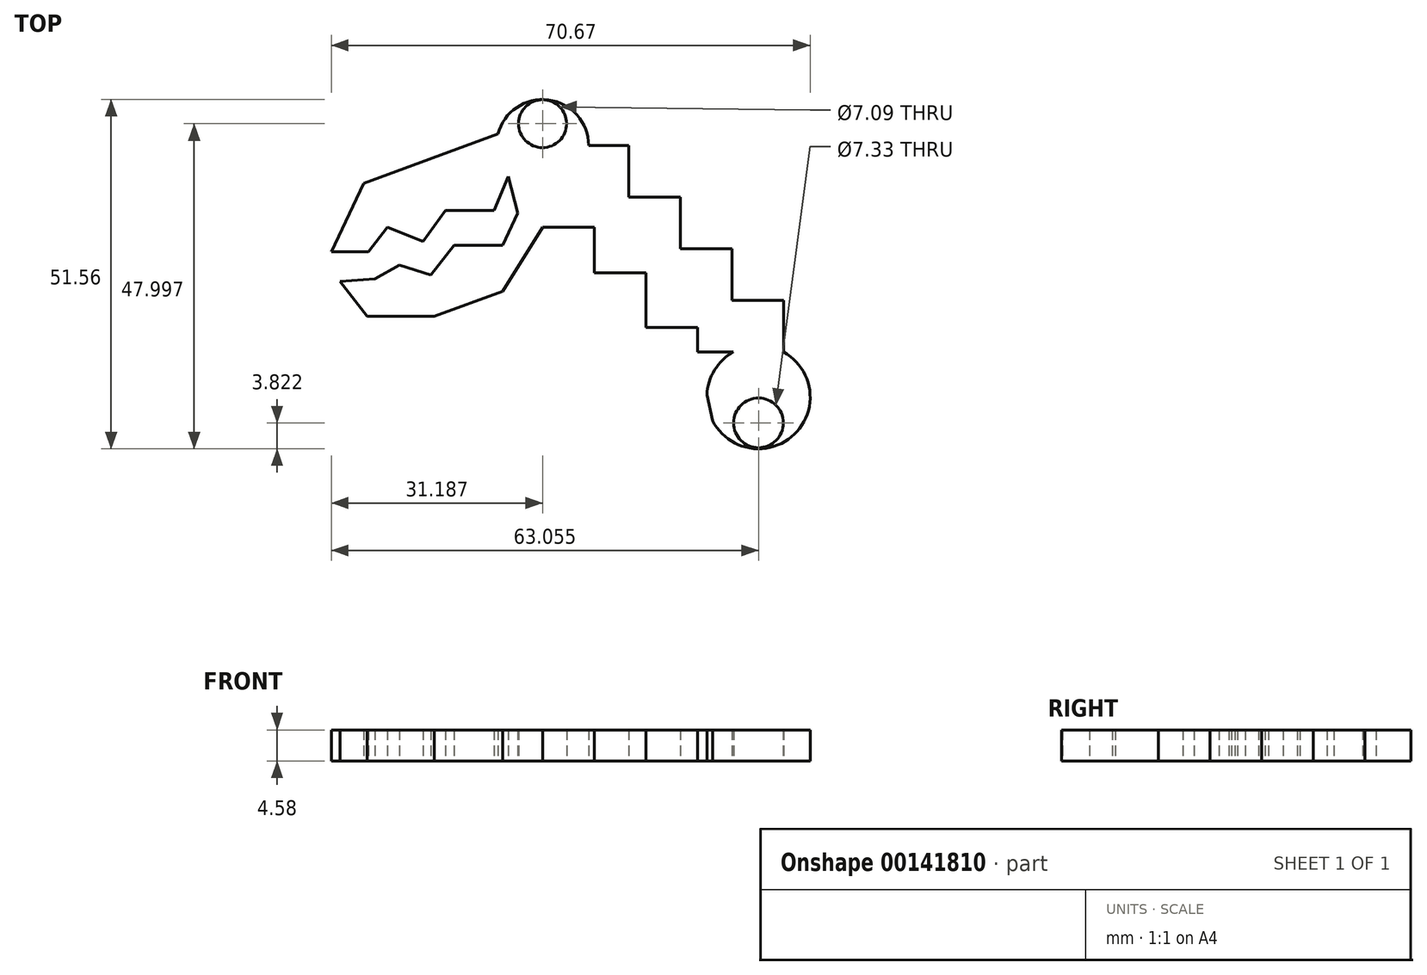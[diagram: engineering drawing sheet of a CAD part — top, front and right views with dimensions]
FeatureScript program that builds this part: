
annotation { "Feature Type Name" : "Feature", "Feature Type Description" : "" }
export const myFeature = defineFeature(function(context is Context, id is Id, definition is map)
    precondition{}
    {
        {
            var Q0;
            Q0=qCreatedBy(makeId("Top.planeOp"),FACE);
            var sketch = newSketch(context, id + "F0", { "sketchPlane" : qUnion([Q0])});
            skLineSegment(sketch, "E0", {"start": v(6.99, 43.15) * mm, "end": v(6.99, 35.53) * mm});
            skLineSegment(sketch, "E1", {"start": v(6.99, 35.53) * mm, "end": v(14.6, 35.53) * mm});
            skLineSegment(sketch, "E2", {"start": v(14.6, 35.53) * mm, "end": v(14.6, 27.9) * mm});
            skLineSegment(sketch, "E3", {"start": v(14.6, 27.9) * mm, "end": v(22.23, 27.9) * mm});
            skLineSegment(sketch, "E4", {"start": v(22.23, 27.9) * mm, "end": v(22.23, 20.29) * mm});
            skLineSegment(sketch, "E5", {"start": v(22.23, 20.29) * mm, "end": v(29.85, 20.29) * mm});
            skLineSegment(sketch, "E6", {"start": v(29.85, 20.29) * mm, "end": v(29.85, 12.67) * mm});
            skLineSegment(sketch, "E7", {"start": v(29.85, 12.67) * mm, "end": v(-5.71, 12.67) * mm});
            skLineSegment(sketch, "E8", {"start": v(-5.71, 12.67) * mm, "end": v(-5.71, 43.15) * mm});
            skLineSegment(sketch, "E9", {"start": v(-5.71, 43.15) * mm, "end": v(6.99, 43.15) * mm});
            skLineSegment(sketch, "E10", {"start": v(-5.71, 31.07) * mm, "end": v(1.9, 31.07) * mm});
            skLineSegment(sketch, "E11", {"start": v(1.9, 31.07) * mm, "end": v(1.9, 24.38) * mm});
            skLineSegment(sketch, "E12", {"start": v(1.9, 24.38) * mm, "end": v(9.53, 24.38) * mm});
            skLineSegment(sketch, "E13", {"start": v(9.53, 24.38) * mm, "end": v(9.53, 16.32) * mm});
            skLineSegment(sketch, "E14", {"start": v(9.53, 16.32) * mm, "end": v(17.15, 16.32) * mm});
            skLineSegment(sketch, "E15", {"start": v(17.15, 16.32) * mm, "end": v(17.15, 12.67) * mm});
            skLineSegment(sketch, "E16", {"start": v(17.15, 12.67) * mm, "end": v(-5.71, 12.67) * mm});
            skArc(sketch, "E17", {"start": v(29.85, 12.67) * mm, "mid": v(26.15, -1.62) * mm, "end": v(22.46, 12.67) * mm});
            skLineSegment(sketch, "E18", {"start": v(17.15, 12.67) * mm, "end": v(19.37, 2.54) * mm});
            skLineSegment(sketch, "E19", {"start": v(19.37, 2.54) * mm, "end": v(17.15, 12.67) * mm});
            skCircle(sketch, "E20", {"center": v(-5.71, 43.15) * mm, "radius": 6.8 * mm});
            skCircle(sketch, "E21", {"center": v(-5.71, 46.38) * mm, "radius": 3.54 * mm});
            skCircle(sketch, "E22", {"center": v(26.15, 2.2) * mm, "radius": 3.67 * mm});
            skPoint(sketch, "E22.centerSnap0", {"position": v(26.15, -1.62) * mm});
            skLineSegment(sketch, "E23", {"start": v(-12.3, 44.84) * mm, "end": v(-32.13, 37.58) * mm});
            skLineSegment(sketch, "E24", {"start": v(-32.13, 37.58) * mm, "end": v(-36.9, 27.5) * mm});
            skLineSegment(sketch, "E25", {"start": v(-36.9, 27.5) * mm, "end": v(-31.4, 27.5) * mm});
            skLineSegment(sketch, "E26", {"start": v(-31.4, 27.5) * mm, "end": v(-28.65, 31.07) * mm});
            skLineSegment(sketch, "E27", {"start": v(-28.65, 31.07) * mm, "end": v(-23.34, 28.96) * mm});
            skLineSegment(sketch, "E28", {"start": v(-23.34, 28.96) * mm, "end": v(-20.04, 33.55) * mm});
            skLineSegment(sketch, "E29", {"start": v(-20.04, 33.55) * mm, "end": v(-12.89, 33.55) * mm});
            skLineSegment(sketch, "E30", {"start": v(-12.89, 33.55) * mm, "end": v(-10.76, 38.6) * mm});
            skLineSegment(sketch, "E31", {"start": v(-10.76, 38.6) * mm, "end": v(-9.4, 33.18) * mm});
            skLineSegment(sketch, "E32", {"start": v(-9.4, 33.18) * mm, "end": v(-11.6, 28.41) * mm});
            skLineSegment(sketch, "E33", {"start": v(-11.6, 28.41) * mm, "end": v(-18.75, 28.41) * mm});
            skLineSegment(sketch, "E34", {"start": v(-18.75, 28.41) * mm, "end": v(-22.24, 24.01) * mm});
            skLineSegment(sketch, "E35", {"start": v(-22.24, 24.01) * mm, "end": v(-26.82, 25.48) * mm});
            skLineSegment(sketch, "E36", {"start": v(-26.82, 25.48) * mm, "end": v(-30.48, 23.46) * mm});
            skLineSegment(sketch, "E37", {"start": v(-30.48, 23.46) * mm, "end": v(-35.62, 23.1) * mm});
            skLineSegment(sketch, "E38", {"start": v(-35.62, 23.1) * mm, "end": v(-31.58, 17.97) * mm});
            skLineSegment(sketch, "E39", {"start": v(-31.58, 17.97) * mm, "end": v(-21.69, 17.97) * mm});
            skLineSegment(sketch, "E40", {"start": v(-21.69, 17.97) * mm, "end": v(-11.6, 21.63) * mm});
            skLineSegment(sketch, "E41", {"start": v(-11.6, 21.63) * mm, "end": v(-5.71, 31.07) * mm});
            skSolve(sketch);
        }
        {
            var Q0;
            {var subQ0=sQuery(id+"F0.wireOp",EDGE,"E23");Q0=makeQuery(id+"F0.imprint","IMPRINT",FACE,{"disambiguationData":[TD([[makeQuery(id+"F0.imprint","IMPRINT",EDGE,{"derivedFrom":subQ0}),1.0]])]});}
            var Q1;
            {var subQ0=sQuery(id+"F0.wireOp",EDGE,"E31");Q1=makeQuery(id+"F0.imprint","IMPRINT",FACE,{"disambiguationData":[TD([[makeQuery(id+"F0.imprint","IMPRINT",EDGE,{"derivedFrom":subQ0}),1.0]])]});}
            var Q2;
            {var subQ0=sQuery(id+"F0.wireOp",EDGE,"E20");var subQ4=sQuery(id+"F0.wireOp",EDGE,"E8");var subQ9=makeQuery(id+"F0.imprint","INTERSECT",VERTEX,{"derivedFrom":[subQ4,subQ0]});Q2=makeQuery(id+"F0.imprint","IMPRINT",FACE,{"disambiguationData":[TD([[makeQuery(id+"F0.imprint","IMPRINT",EDGE,{"disambiguationData":[TD([[subQ9,-1.0]])],"derivedFrom":subQ4}),1.0]])]});}
            var Q3;
            {var subQ0=sQuery(id+"F0.wireOp",EDGE,"E20");var subQ1=sQuery(id+"F0.wireOp",EDGE,"E8");var subQ2=makeQuery(id+"F0.imprint","INTERSECT",VERTEX,{"derivedFrom":[subQ1,subQ0]});Q3=makeQuery(id+"F0.imprint","IMPRINT",FACE,{"disambiguationData":[TD([[makeQuery(id+"F0.imprint","IMPRINT",EDGE,{"disambiguationData":[TD([[subQ2,-1.0]])],"derivedFrom":subQ1}),-1.0]])]});}
            var Q4;
            {var subQ4=sQuery(id+"F0.wireOp",EDGE,"E0");Q4=makeQuery(id+"F0.imprint","IMPRINT",FACE,{"disambiguationData":[TD([[makeQuery(id+"F0.imprint","IMPRINT",EDGE,{"derivedFrom":subQ4}),-1.0]])]});}
            var Q5;
            Q5=makeQuery(id+"F0.imprint","IMPRINT",FACE,{"disambiguationData":[TD([[makeQuery(id+"F0.imprint","IMPRINT",EDGE,{"derivedFrom":sQuery(id+"F0.wireOp",EDGE,"E22")}),-1.0]])]});
            var Q6;
            {var subQ1=sQuery(id+"F0.wireOp",EDGE,"E7");var subQ3=sQuery(id+"F0.wireOp",EDGE,"E17");var subQ4=makeQuery(id+"F0.imprint","INTERSECT",VERTEX,{"derivedFrom":[subQ1,subQ3]});Q6=makeQuery(id+"F0.imprint","IMPRINT",FACE,{"disambiguationData":[TD([[makeQuery(id+"F0.imprint","IMPRINT",EDGE,{"disambiguationData":[TD([[subQ4,1.0]])],"derivedFrom":subQ3}),1.0]])]});}
            extrude(context, id + "F1", {"entities" : qUnion([Q0, Q1, Q2, Q3, Q4, Q5, Q6]), "depth" : 2.3 * mm, "hasSecondDirection" : true, "secondDirectionOppositeDirection" : true, "secondDirectionDepth" : 2.3 * mm});
        }
    });
